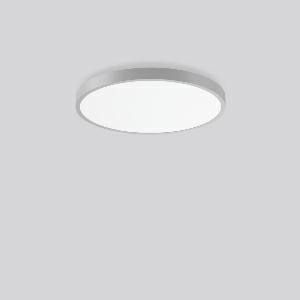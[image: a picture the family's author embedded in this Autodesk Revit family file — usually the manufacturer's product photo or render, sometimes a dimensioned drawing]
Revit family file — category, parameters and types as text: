
# Revit family: triona_round_a_312383_004_76_a57e
name_source: partatom
category: Lighting Fixtures
units: mm (PartAtom-declared; Revit-internal decimal feet)

## family parameters
Cut with Voids When Loaded = No
Host = Face
Light Source = No
Part Type = Normal
Room Calculation Point = No
Round Connector Dimension = Use Diameter
Shared = No

## types (1)
- TRIONA round A (1 x LED Modul 830, 6450 lm, 3000)
    Apparent Load = 70 VA
    CIE Flux Codes = 49 80 96 100 100
    Color Rendering = 80
    Color Temperature = 3000
    Default Elevation = 1800 mm
    Description = Series: TRIONA round
Decorative round LED surface-mounted luminaire. Flat, seamless frame: aluminium extrusion profile, powder coated. Cover made of sheet steel, powder-coated. Light emission through a diffuser: plastic, opal. Lightguide and diffuser made of non-yellowing plastic (PMMA). Lateral light emission (RZB SIDELITE technology) for above-average homogeneous light distribution. Suitable for Ceiling mounting, Wall (surface). Tool-free mounting via bayonet connection. Electronic ballast included. Very easy installation thanks to Plug+Play connection. 
Colour: silver, matt (approx. RAL 9006)
Diameter: 681 mm
Height: 88 mm
Lamp: LED
Socket: without socket
Colour temperature: 3000K
Colour rendering index (CRI): 80
System power: 70 W
Rated luminous flux: 6450 lm
Luminous efficiency: 92 lm/W
Control gear: Converter, dimmable, DALI
Protection class: I
Type of protection: IP 20
    Height = 88 mm
    Lamp = 1 x LED Modul 830
    Lamp Light Flux = 6450 lm
    Lamp count = 1
    Length = 681 mm
    Lifetime = 50000 h
    Luminous efficacy = 92 lm/W
    Manufacturer = RZB
    ModVariant = No
    Model = 312383.004.76
    Mounting Place = Ceiling
    Mounting Type = Surface mounted
    Number of Poles = 1
    OnlyDefault = Yes
    Power Factor = 1
    Product Name = TRIONA round A
    Product group = Surface mounted modular luminaires
    ProductGroupID = 306
    Protection Class = Protection class I
    Protection Degree = IP 20
    RLX_Detail_Level = 1
    RLX_Emergency_Light_Flux = 0 lm
    RLX_Emergency_Type = 0
    RLX_Emergency_Type_DB = No
    RlxData = <blob elided: 31661 chars, md5=c4a0796a>
    Socket = socket
    Standby Power = 0 W
    System Light Flux = 6450 lm
    System Power = 70 W
    Type Comments = Product without accessories
    Type Image = 312384.004.jpg
    URL = http://relux.com
    VarID = ---
    Voltage = 230 V
    Voltage Range = 220-240 V
    Weight = 0.00 kg
    Width = 0 mm  [stored 0 ft]

note: [stored X ft] marks values corroborated as IEEE doubles in the binary element streams (Revit-internal decimal feet)

## geometry (parser evidence)
native form markers: Blend x4, Sweep x9
no freeform markers — native parametric forms only
